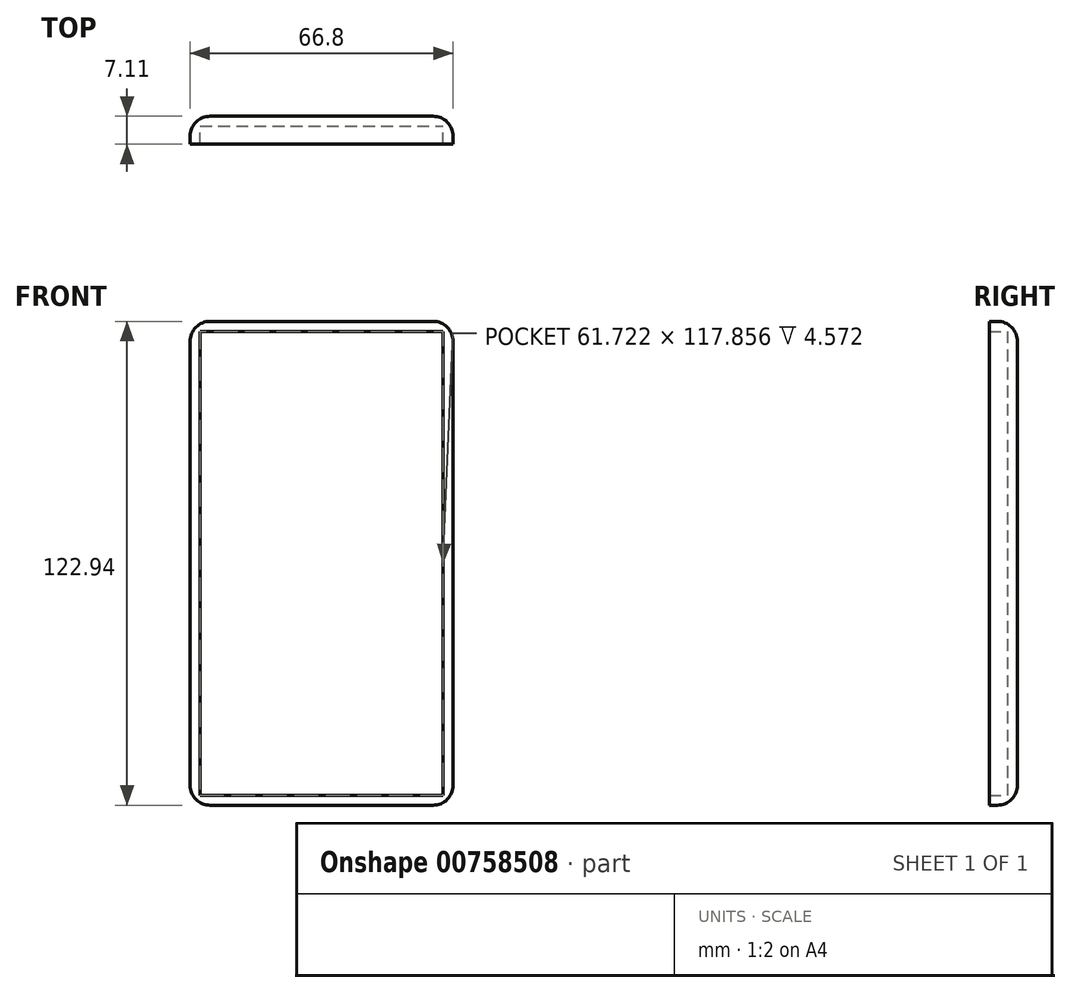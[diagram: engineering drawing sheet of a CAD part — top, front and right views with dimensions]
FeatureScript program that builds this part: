
annotation { "Feature Type Name" : "Feature", "Feature Type Description" : "" }
export const myFeature = defineFeature(function(context is Context, id is Id, definition is map)
    precondition{}
    {
        {
            var Q0;
            Q0=qCreatedBy(makeId("Front.planeOp"),FACE);
            var sketch = newSketch(context, id + "F0", { "sketchPlane" : qUnion([Q0])});
            skLineSegment(sketch, "E0.bottom", {"start": v(-33.4, 61.47) * mm, "end": v(33.4, 61.47) * mm});
            skLineSegment(sketch, "E0.top", {"start": v(-33.4, -61.47) * mm, "end": v(33.4, -61.47) * mm});
            skLineSegment(sketch, "E0.left", {"start": v(-33.4, 61.47) * mm, "end": v(-33.4, -61.47) * mm});
            skLineSegment(sketch, "E0.right", {"start": v(33.4, 61.47) * mm, "end": v(33.4, -61.47) * mm});
            skPoint(sketch, "E0.middle", {"position": v(0, 0) * mm});
            skSolve(sketch);
        }
        {
            var Q0;
            Q0=makeQuery(id+"F0.imprint","IMPRINT",FACE,{"disambiguationData":[TD([[makeQuery(id+"F0.imprint","IMPRINT",EDGE,{"derivedFrom":sQuery(id+"F0.wireOp",EDGE,"E0.bottom")}),-1.0]])]});
            extrude(context, id + "F1", {"entities" : qUnion([Q0]), "depth" : 7.11 * mm, "offsetDistance" : 25.4 * mm});
        }
        {
            var Q0;
            Q0=makeQuery(id+"F1.opExtrude","CAP_FACE",FACE,{"disambiguationData":[OSD([sQuery(id+"F0.wireOp",EDGE,"E0.bottom"),sQuery(id+"F0.wireOp",EDGE,"E0.top"),sQuery(id+"F0.wireOp",EDGE,"E0.left"),sQuery(id+"F0.wireOp",EDGE,"E0.right")])],"isStart":false});
            shell(context, id + "F2", {"entities" : qUnion([Q0]), "thickness" : 2.54 * mm});
        }
        {
            var Q0;
            Q0=makeQuery(id+"F1.opExtrude","SWEPT_EDGE",EDGE,{"disambiguationData":[OSD([sQuery(id+"F0.wireOp",EDGE,"E0.bottom"),sQuery(id+"F0.wireOp",EDGE,"E0.right")])]});
            var Q1;
            Q1=makeQuery(id+"F1.opExtrude","SWEPT_EDGE",EDGE,{"disambiguationData":[OSD([sQuery(id+"F0.wireOp",EDGE,"E0.top"),sQuery(id+"F0.wireOp",EDGE,"E0.right")])]});
            var Q2;
            Q2=makeQuery(id+"F1.opExtrude","SWEPT_EDGE",EDGE,{"disambiguationData":[OSD([sQuery(id+"F0.wireOp",EDGE,"E0.top"),sQuery(id+"F0.wireOp",EDGE,"E0.left")])]});
            var Q3;
            Q3=makeQuery(id+"F1.opExtrude","SWEPT_EDGE",EDGE,{"disambiguationData":[OSD([sQuery(id+"F0.wireOp",EDGE,"E0.bottom"),sQuery(id+"F0.wireOp",EDGE,"E0.left")])]});
            var Q4;
            Q4=makeQuery(id+"F1.opExtrude","CAP_EDGE",EDGE,{"disambiguationData":[OSD([sQuery(id+"F0.wireOp",EDGE,"E0.left")])],"isStart":true});
            var Q5;
            Q5=makeQuery(id+"F1.opExtrude","CAP_EDGE",EDGE,{"disambiguationData":[OSD([sQuery(id+"F0.wireOp",EDGE,"E0.bottom")])],"isStart":true});
            var Q6;
            Q6=makeQuery(id+"F1.opExtrude","CAP_EDGE",EDGE,{"disambiguationData":[OSD([sQuery(id+"F0.wireOp",EDGE,"E0.right")])],"isStart":true});
            var Q7;
            Q7=makeQuery(id+"F1.opExtrude","CAP_EDGE",EDGE,{"disambiguationData":[OSD([sQuery(id+"F0.wireOp",EDGE,"E0.top")])],"isStart":true});
            fillet(context, id + "F3", {"entities" : qUnion([Q0, Q1, Q2, Q3, Q4, Q5, Q6, Q7]), "radius" : 5.08 * mm, "tangentPropagation" : true, "allowEdgeOverflow" : false});
        }
    });
